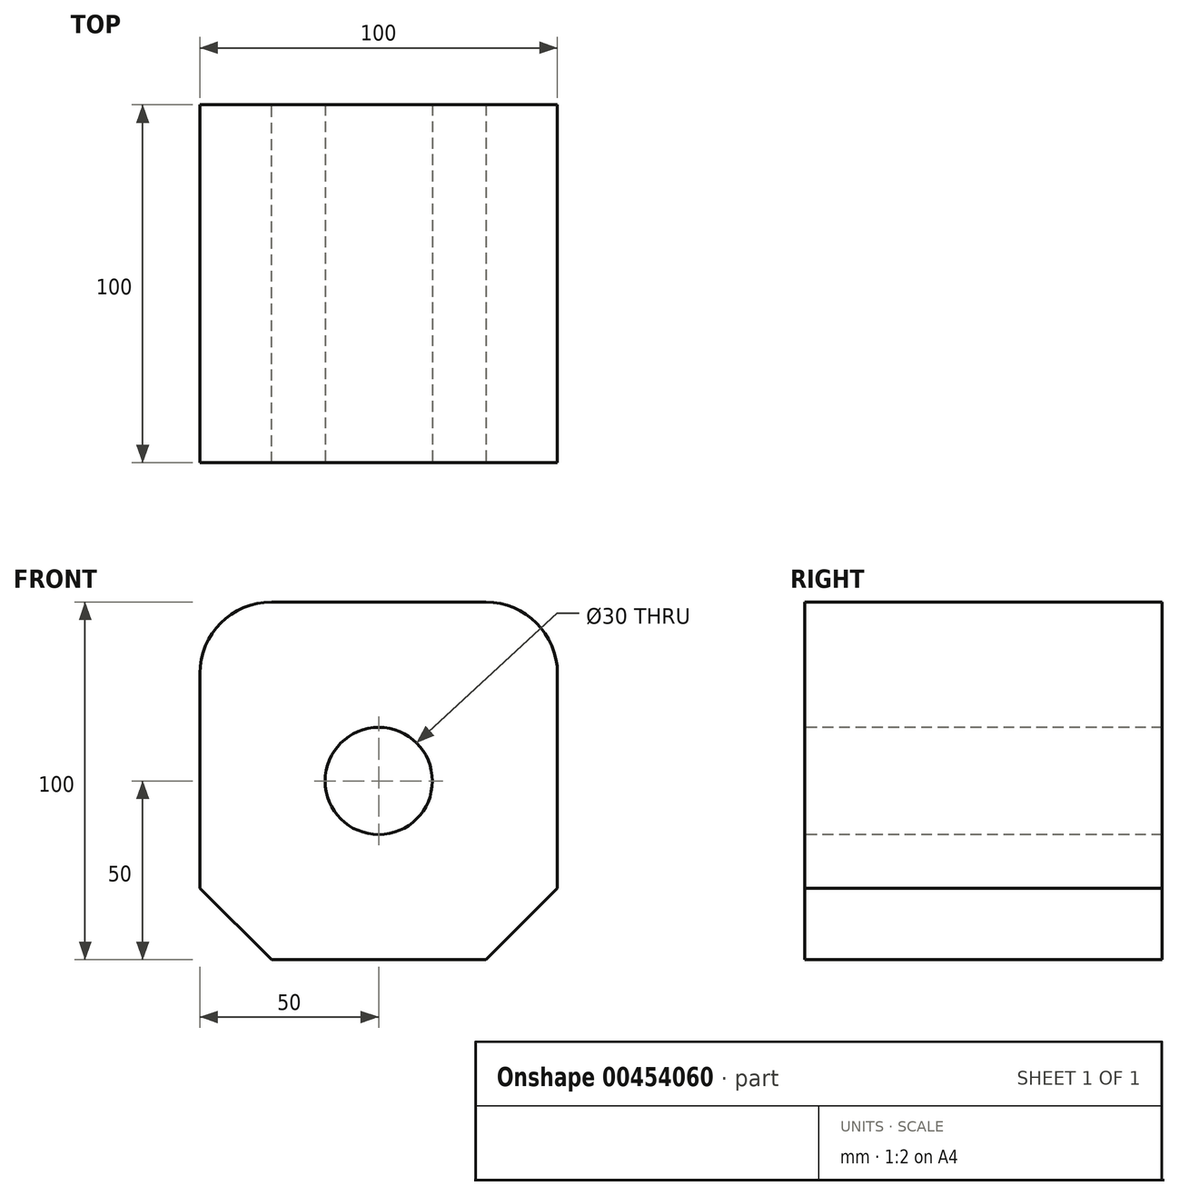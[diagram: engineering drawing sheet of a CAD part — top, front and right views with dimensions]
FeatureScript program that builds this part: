
annotation { "Feature Type Name" : "Feature", "Feature Type Description" : "" }
export const myFeature = defineFeature(function(context is Context, id is Id, definition is map)
    precondition{}
    {
        {
            var Q0;
            Q0=qCreatedBy(makeId("Front.planeOp"),FACE);
            var sketch = newSketch(context, id + "F0", { "sketchPlane" : qUnion([Q0])});
            skLineSegment(sketch, "E0.bottom", {"start": v(50, -50) * mm, "end": v(-50, -50) * mm});
            skLineSegment(sketch, "E0.top", {"start": v(50, 50) * mm, "end": v(-50, 50) * mm});
            skLineSegment(sketch, "E0.left", {"start": v(50, -50) * mm, "end": v(50, 50) * mm});
            skLineSegment(sketch, "E0.right", {"start": v(-50, -50) * mm, "end": v(-50, 50) * mm});
            skPoint(sketch, "E0.middle", {"position": v(0, 0) * mm});
            skSolve(sketch);
        }
        {
            var Q0;
            Q0 = qSketchRegion(id + "F0", true);
            extrude(context, id + "F1", {"entities" : qUnion([Q0]), "depth" : 100 * mm});
        }
        {
            var Q0;
            Q0=makeQuery(id+"F1.opExtrude","SWEPT_EDGE",EDGE,{"disambiguationData":[OSD([sQuery(id+"F0.wireOp",EDGE,"E0.top"),sQuery(id+"F0.wireOp",EDGE,"E0.right")])]});
            var Q1;
            Q1=makeQuery(id+"F1.opExtrude","SWEPT_EDGE",EDGE,{"disambiguationData":[OSD([sQuery(id+"F0.wireOp",EDGE,"E0.top"),sQuery(id+"F0.wireOp",EDGE,"E0.left")])]});
            fillet(context, id + "F2", {"entities" : qUnion([Q0, Q1]), "radius" : 20 * mm, "tangentPropagation" : true, "allowEdgeOverflow" : false});
        }
        {
            var Q0;
            Q0=makeQuery(id+"F1.opExtrude","SWEPT_EDGE",EDGE,{"disambiguationData":[OSD([sQuery(id+"F0.wireOp",EDGE,"E0.bottom"),sQuery(id+"F0.wireOp",EDGE,"E0.left")])]});
            var Q1;
            Q1=makeQuery(id+"F1.opExtrude","SWEPT_EDGE",EDGE,{"disambiguationData":[OSD([sQuery(id+"F0.wireOp",EDGE,"E0.bottom"),sQuery(id+"F0.wireOp",EDGE,"E0.right")])]});
            chamfer(context, id + "F3", {"entities" : qUnion([Q0, Q1]), "width" : 20 * mm, "tangentPropagation" : true});
        }
        {
            var Q0;
            Q0=makeQuery(id+"F1.opExtrude","CAP_FACE",FACE,{"disambiguationData":[OSD([sQuery(id+"F0.wireOp",EDGE,"E0.bottom"),sQuery(id+"F0.wireOp",EDGE,"E0.top"),sQuery(id+"F0.wireOp",EDGE,"E0.left"),sQuery(id+"F0.wireOp",EDGE,"E0.right")])],"isStart":false});
            var sketch = newSketch(context, id + "F4", { "sketchPlane" : qUnion([Q0])});
            skCircle(sketch, "E1", {"center": v(0, 0) * mm, "radius": 15 * mm});
            skSolve(sketch);
        }
        {
            var Q0;
            Q0=makeQuery(id+"F4.imprint","IMPRINT",FACE,{"disambiguationData":[TD([[makeQuery(id+"F4.imprint","IMPRINT",EDGE,{"derivedFrom":sQuery(id+"F4.wireOp",EDGE,"E1")}),1.0]])]});
            extrude(context, id + "F5", {"entities" : qUnion([Q0]), "operationType" : NewBodyOperationType.REMOVE, "endBound" : BoundingType.THROUGH_ALL, "oppositeDirection" : true, "depth" : 25 * mm});
        }
    });
